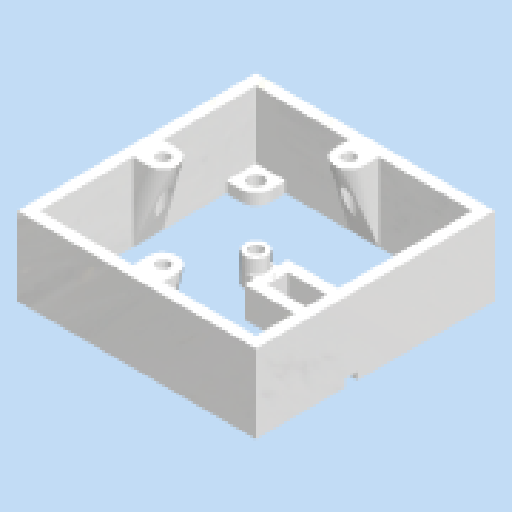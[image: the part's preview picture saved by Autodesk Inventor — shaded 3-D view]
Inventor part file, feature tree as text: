
AUTODESK INVENTOR PART (.ipt)
format: ipt  version: 2024 (Build 280153000, 153)  size: 527,360 bytes
history: native  units: in
note: dims shown in document units (in); Inventor stores cm internally (conversion verified against a paired STEP export)
features: sketch x9, extrude x6, pattern_circular x2, other x2, hole x2, plane x2, projected_geometry x2, chamfer x1, loft x1
ambient origin geometry x8: Origin, YZ Plane, XZ Plane, XY Plane, X Axis, Y Axis, Z Axis, Center Point
bodies: Body1 (feature_tree)
feature tree (27):
  extrude  "Extrusion3"  Depth=4.0in
  extrude  "Extrusion4"  Depth=0.1875in TaperAngle=0.0deg
  pattern_circular  "Circular Pattern1"  Count=4 Angle=360.0deg
  extrude  "Extrusion5"  Depth=0.2in
  chamfer  "Chamfer1"  Distance=3.625in
  other  "Work Axis1"
  extrude  "Extrusion9"  Depth=0.2in TaperAngle=0.0deg
  extrude  "Extrusion10"  Depth=0.2in
  other  "Work Point1"
  hole  "Hole1"  [1 undecoded]
  loft  "Loft1"
  hole  "Hole2"  [1 undecoded]
  pattern_circular  "Circular Pattern2"  [2 undecoded]
  extrude  "Extrusion11"  Depth=0.2in
  sketch  "Sketch3"  dims[d17=4.0in d18=4.0in]
  sketch  "Sketch4"  dims[d19=0.1875in d20=1.3125in d21=0.0in]
  sketch  "Sketch5"  dims[d22=4.0in]
  plane  "Work Plane2"
  plane  "Work Plane3"
  sketch  "Sketch9"  dims[d23=4.0in]
  sketch  "Sketch10"  dims[d24=0.1875in]
  sketch  "Sketch11"  dims[d25=0.25in]
  projected_geometry  "Projected Loop3"
  sketch  "Sketch12"  dims[d26=0.125in]
  sketch  "Sketch13"  dims[d27=0.1875in d28=0.0in d30=1.5748in d31=360.0deg]
  projected_geometry  "Projected Loop5"
  sketch  "Sketch14"  dims[d33=0.1378in d34=0.7874in d35=3.625in d36=0.5118in d37=0.0in d38=0.0079in d39=0.1875in d69=0.375in d70=0.125in d71=45.0deg d72=1.0in d73=0.1555in d74=0.3346in d75=0.25in d76=0.0394in d77=0.1225in d78=0.7874in d80=180.0deg d82=0.375in d83=0.375in d84=0.25in d85=0.0in d86=0.375in d87=0.2382in d88=0.0in d89=1.0in d90=1.0in d91=0.201in d92=0.75in d93=0.375in d94=0.25in d95=0.5635in d96=1.0in d97=0.8108in d98=0.5in d99=0.5in d100=0.25in d101=0.0in d102=90.0deg d103=0.0in d104=90.0deg d105=0.21in d106=0.75in d107=0.375in d108=0.25in d109=0.5635in d110=1.0in d111=0.8108in d112=1.1811in d113=180.0deg d115=0.2in d116=0.125in d117=0.2in d118=0.0in d16=0.0312in]
note: 4 required parameter values undecoded (feature->parameter linkage not recoverable at this tier; creation-order binding heuristic only, values carry confidence <= 0.55)
